# Revit family: QF_COMENDA_CE60
name_source: partatom
category: Attrezzature speciali
units: mm (PartAtom-declared; Revit-internal decimal feet)

## family parameters
Basato su piano di lavoro = No
Condiviso = No
Numero OmniClass = 23.40.40.14
Punto di calcolo locali = No
Quota connettore circolare = Usa diametro
Sempre verticale = Sì
Taglio con vuoti quando caricato = No
Tipo di parte = Normale
Titolo OmniClass = Food Service Equipment

## types (3) — shared parameters
Altezza = 820 mm  [stored 2.69029 ft]
Altezza allacciamento elettrico da pavimento finito = 55 mm  [stored 0.180446 ft]
Altezza da terra raccordo acqua calda = 55 mm  [stored 0.180446 ft]
Altezza dello scarico diretto acqua da pavimento finito = 55 mm  [stored 0.180446 ft]
Corrente di funzionamento normale = 11 A
Diametro dello scarico diretto di acqua = 1 1/2"
Diametro raccordo acqua calda = 1"
Fase = 3
Frequenza = 50 Hz
Lunghezza = 600 mm
Numero dei poli = 3
Peso netto = 58.00 kg
Potenza elettrica = 5450 W
Pressione minima acqua calda = 2000.0 Pa
Produttore = HOONVED
Profondità = 605 mm  [stored 1.98491 ft]
Protezione contro le sovracorrenti = 16 A
Temperatura raccomandata per acqua calda = 50 °C
Tensione = 400 V
URL = https://www.hoonved.com
URL catalogo = https://www.hoonved.com

## per-type parameters (varying)
| type | Descrizione | Modello |
| H56500 | MULTIPOWER DISHWASHER | CE60 |
| H56502 | MULTIPOWER DISHWASHER WITH WATER SOFTENER | CE60D |
| H56520 | MULTIPOWER DISHWASHER WITH BREAK TANK | CE60BT |

note: [stored X ft] marks values corroborated as IEEE doubles in the binary element streams (Revit-internal decimal feet)

## geometry (parser evidence)
native form markers: Sweep x5
no freeform markers — native parametric forms only
